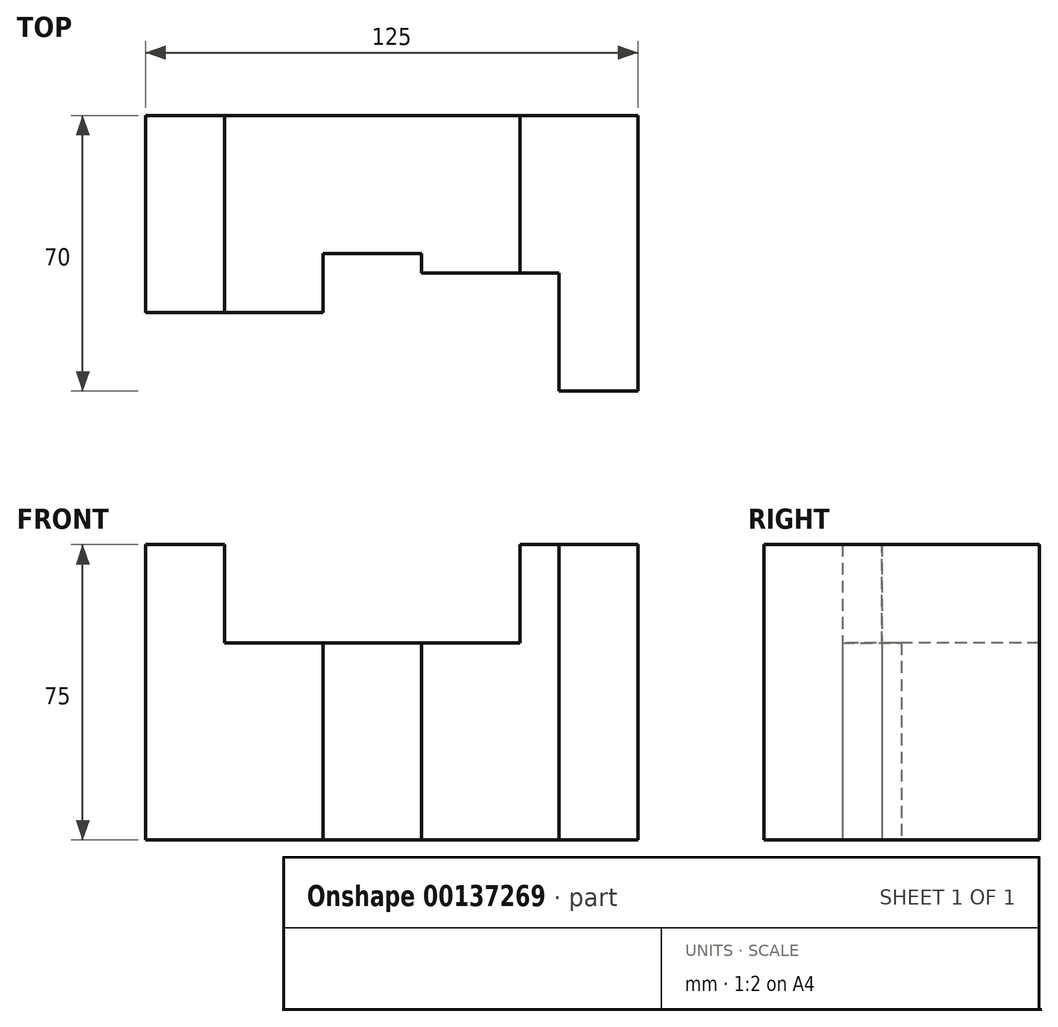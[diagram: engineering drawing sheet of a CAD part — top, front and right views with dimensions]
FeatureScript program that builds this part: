
annotation { "Feature Type Name" : "Feature", "Feature Type Description" : "" }
export const myFeature = defineFeature(function(context is Context, id is Id, definition is map)
    precondition{}
    {
        {
            var Q0;
            Q0=qCreatedBy(makeId("Top.planeOp"),FACE);
            var sketch = newSketch(context, id + "F0", { "sketchPlane" : qUnion([Q0])});
            skLineSegment(sketch, "E0", {"start": v(0, 0) * mm, "end": v(0, 50) * mm});
            skLineSegment(sketch, "E1", {"start": v(0, 50) * mm, "end": v(125, 50) * mm});
            skLineSegment(sketch, "E2", {"start": v(125, 50) * mm, "end": v(125, -20) * mm});
            skLineSegment(sketch, "E3", {"start": v(125, -20) * mm, "end": v(105, -20) * mm});
            skLineSegment(sketch, "E4", {"start": v(105, -20) * mm, "end": v(105, 10) * mm});
            skLineSegment(sketch, "E5", {"start": v(105, 10) * mm, "end": v(70, 10) * mm});
            skLineSegment(sketch, "E6", {"start": v(70, 10) * mm, "end": v(70, 15) * mm});
            skLineSegment(sketch, "E7", {"start": v(70, 15) * mm, "end": v(45, 15) * mm});
            skLineSegment(sketch, "E8", {"start": v(45, 15) * mm, "end": v(45, 0) * mm});
            skLineSegment(sketch, "E9", {"start": v(45, 0) * mm, "end": v(0, 0) * mm});
            skSolve(sketch);
        }
        {
            var Q0;
            Q0=makeQuery(id+"F0.imprint","IMPRINT",FACE,{"disambiguationData":[TD([[makeQuery(id+"F0.imprint","IMPRINT",EDGE,{"derivedFrom":sQuery(id+"F0.wireOp",EDGE,"E0")}),-1.0]])]});
            extrude(context, id + "F1", {"entities" : qUnion([Q0]), "depth" : 75 * mm});
        }
        {
            var Q0;
            Q0=makeQuery(id+"F1.opExtrude","SWEPT_FACE",FACE,{"disambiguationData":[OSD([sQuery(id+"F0.wireOp",EDGE,"E9")])]});
            var sketch = newSketch(context, id + "F2", { "sketchPlane" : qUnion([Q0])});
            skLineSegment(sketch, "E10.0", {"start": v(45, 75) * mm, "end": v(0, 75) * mm});
            skLineSegment(sketch, "E11.0", {"start": v(105, 75) * mm, "end": v(70, 75) * mm});
            skLineSegment(sketch, "E12", {"start": v(20, 75) * mm, "end": v(20, 50) * mm});
            skLineSegment(sketch, "E13", {"start": v(20, 50) * mm, "end": v(95, 50) * mm});
            skLineSegment(sketch, "E14", {"start": v(95, 50) * mm, "end": v(95, 75) * mm});
            skLineSegment(sketch, "E15.0", {"start": v(70, 75) * mm, "end": v(45, 75) * mm});
            skSolve(sketch);
        }
        {
            var Q0;
            {var subQ1=sQuery(id+"F2.wireOp",EDGE,"E14");Q0=makeQuery(id+"F2.imprint","IMPRINT",FACE,{"disambiguationData":[TD([[makeQuery(id+"F2.imprint","IMPRINT",EDGE,{"derivedFrom":subQ1}),1.0]])]});}
            var Q1;
            {var subQ3=sQuery(id+"F2.wireOp",EDGE,"E12");Q1=makeQuery(id+"F2.imprint","IMPRINT",FACE,{"disambiguationData":[TD([[makeQuery(id+"F2.imprint","IMPRINT",EDGE,{"derivedFrom":subQ3}),1.0]])]});}
            extrude(context, id + "F3", {"entities" : qUnion([Q0, Q1]), "operationType" : NewBodyOperationType.REMOVE, "endBound" : BoundingType.THROUGH_ALL, "oppositeDirection" : true, "depth" : 25 * mm});
        }
    });
